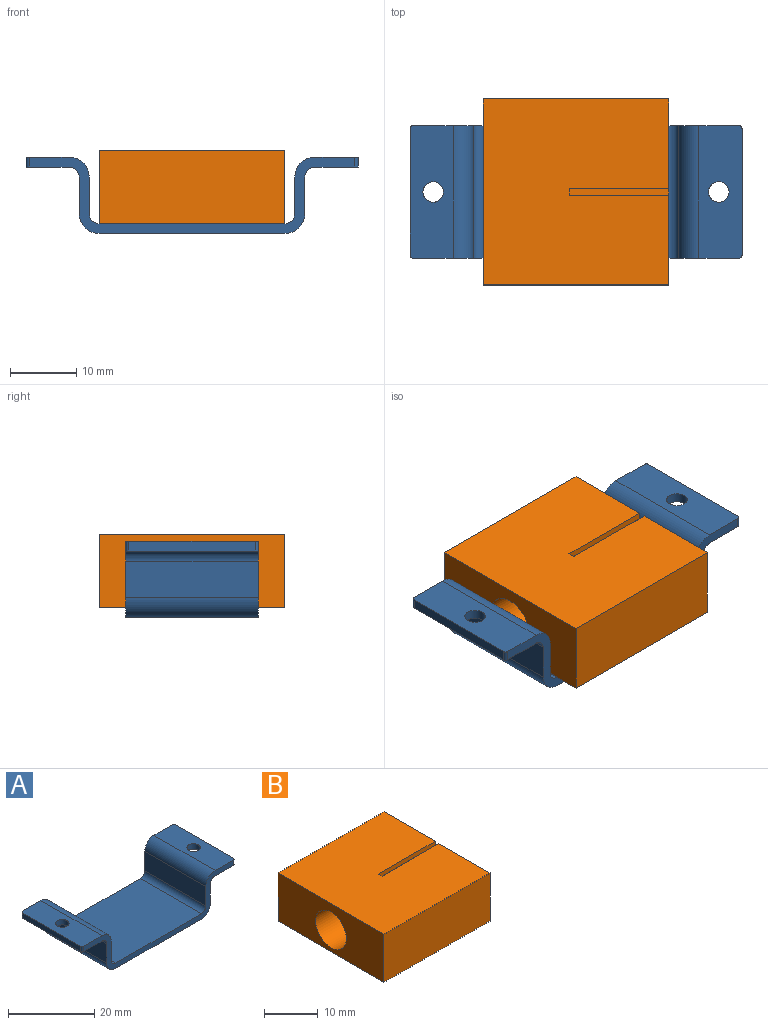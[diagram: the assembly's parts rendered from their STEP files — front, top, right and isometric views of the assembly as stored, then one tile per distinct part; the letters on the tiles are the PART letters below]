
ASSEMBLY  parts=2 mates=1
PART A: 28 faces, bbox 50x20x11.5 mm
  f0: plane 20x6.5mm, normal (0,0,-1), area 122.3mm2, adj f1,f19,f20,f21,f23,f25,f27
  f1: plane 19x1.5mm, normal (1,0,0), area 28.5mm2, adj f0,f2,f25,f27
  f2: plane 20x6.5mm, normal (0,0,1), area 122.3mm2, adj f1,f3,f20,f21,f23,f25,f27
  f3: cylinder r=3mm len=20mm, axis (0,1,0), area 94.2mm2, adj f2,f4,f20,f21
  f4: plane 20x5.5mm, normal (-1,0,0), area 110mm2, adj f3,f5,f20,f21
  f5: cylinder r=1.5mm len=20mm, axis (0,1,0), area 47.1mm2, adj f4,f6,f20,f21
  f6: plane 28x20mm, normal (0,0,1), area 560mm2, adj f5,f7,f20,f21
  f7: cylinder r=1.5mm len=20mm, axis (0,1,0), area 47.1mm2, adj f6,f8,f20,f21
  f8: plane 20x5.5mm, normal (1,0,0), area 110mm2, adj f7,f9,f20,f21
  f9: cylinder r=3mm len=20mm, axis (0,1,0), area 94.2mm2, adj f8,f10,f20,f21
  f10: plane 20x6.5mm, normal (0,0,1), area 122.3mm2, adj f9,f11,f20,f21,f22,f24,f26
  f11: plane 19x1.5mm, normal (-1,0,0), area 28.5mm2, adj f10,f12,f24,f26
  f12: plane 20x6.5mm, normal (0,0,-1), area 122.3mm2, adj f11,f13,f20,f21,f22,f24,f26
  f13: cylinder r=1.5mm len=20mm, axis (0,1,0), area 47.1mm2, adj f12,f14,f20,f21
  f14: plane 20x5.5mm, normal (-1,0,0), area 110mm2, adj f13,f15,f20,f21
  f15: cylinder r=3mm len=20mm, axis (0,1,0), area 94.2mm2, adj f14,f16,f20,f21
  f16: plane 28x20mm, normal (0,0,-1), area 560mm2, adj f15,f17,f20,f21
  f17: cylinder r=3mm len=20mm, axis (0,1,0), area 94.2mm2, adj f16,f18,f20,f21
  f18: plane 20x5.5mm, normal (1,0,0), area 110mm2, adj f17,f19,f20,f21
  f19: cylinder r=1.5mm len=20mm, axis (0,1,0), area 47.1mm2, adj f0,f18,f20,f21
  f20: plane 49x11.5mm, normal (0,-1,0), area 97.7mm2, adj f0,f2,f3,f4,f5,f6,f7,f8
  f21: plane 49x11.5mm, normal (0,1,0), area 97.7mm2, adj f0,f2,f3,f4,f5,f6,f7,f8
  f22: cylinder r=1.55mm len=3.1mm, axis (0,0,1), area 14.6mm2, adj f10,f12
  f23: cylinder r=1.55mm len=3.1mm, axis (0,0,1), area 14.6mm2, adj f0,f2
  f24: cylinder r=0.5mm len=1.5mm, axis (0,0,-1), area 1.2mm2, adj f10,f11,f12,f21
  f25: cylinder r=0.5mm len=1.5mm, axis (0,0,1), area 1.2mm2, adj f0,f1,f2,f21
  f26: cylinder r=0.5mm len=1.5mm, axis (0,0,1), area 1.2mm2, adj f10,f11,f12,f20
  f27: cylinder r=0.5mm len=1.5mm, axis (0,0,-1), area 1.2mm2, adj f0,f1,f2,f20
PART B: 11 faces, bbox 28x28x11 mm
  f0: cylinder r=4.05mm len=28mm, axis (1,0,0), area 712.5mm2, adj f5,f7
  f1: plane 28x28mm, normal (0,0,-1), area 784mm2, adj f4,f5,f6,f7
  f2: plane 15x1mm, normal (0,0,1), area 15mm2, adj f7,f8,f9,f10
  f3: plane 28x28mm, normal (0,0,1), area 769mm2, adj f4,f5,f6,f7,f8,f9,f10
  f4: plane 28x11mm, normal (0,1,0), area 308mm2, adj f1,f3,f5,f7
  f5: plane 28x11mm, normal (-1,0,0), area 256.5mm2, adj f0,f1,f3,f4,f6
  f6: plane 28x11mm, normal (0,-1,0), area 308mm2, adj f1,f3,f5,f7
  f7: plane 28x11mm, normal (1,0,0), area 255.5mm2, adj f0,f1,f2,f3,f4,f6,f8,f9
  f8: plane 15x1mm, normal (0,1,0), area 15mm2, adj f2,f3,f7,f10
  f9: plane 15x1mm, normal (0,-1,0), area 15mm2, adj f2,f3,f7,f10
  f10: plane 1x1mm, normal (1,0,0), area 1mm2, adj f2,f3,f8,f9
PLACE A t=(0.23,0.06,4.4)mm
PLACE B t=(0.23,0.06,-5.6)mm
MATE fastened A.f6 <-> B.f1  axis (0,0,1) through (0.23,0.06,-5.6)mm
